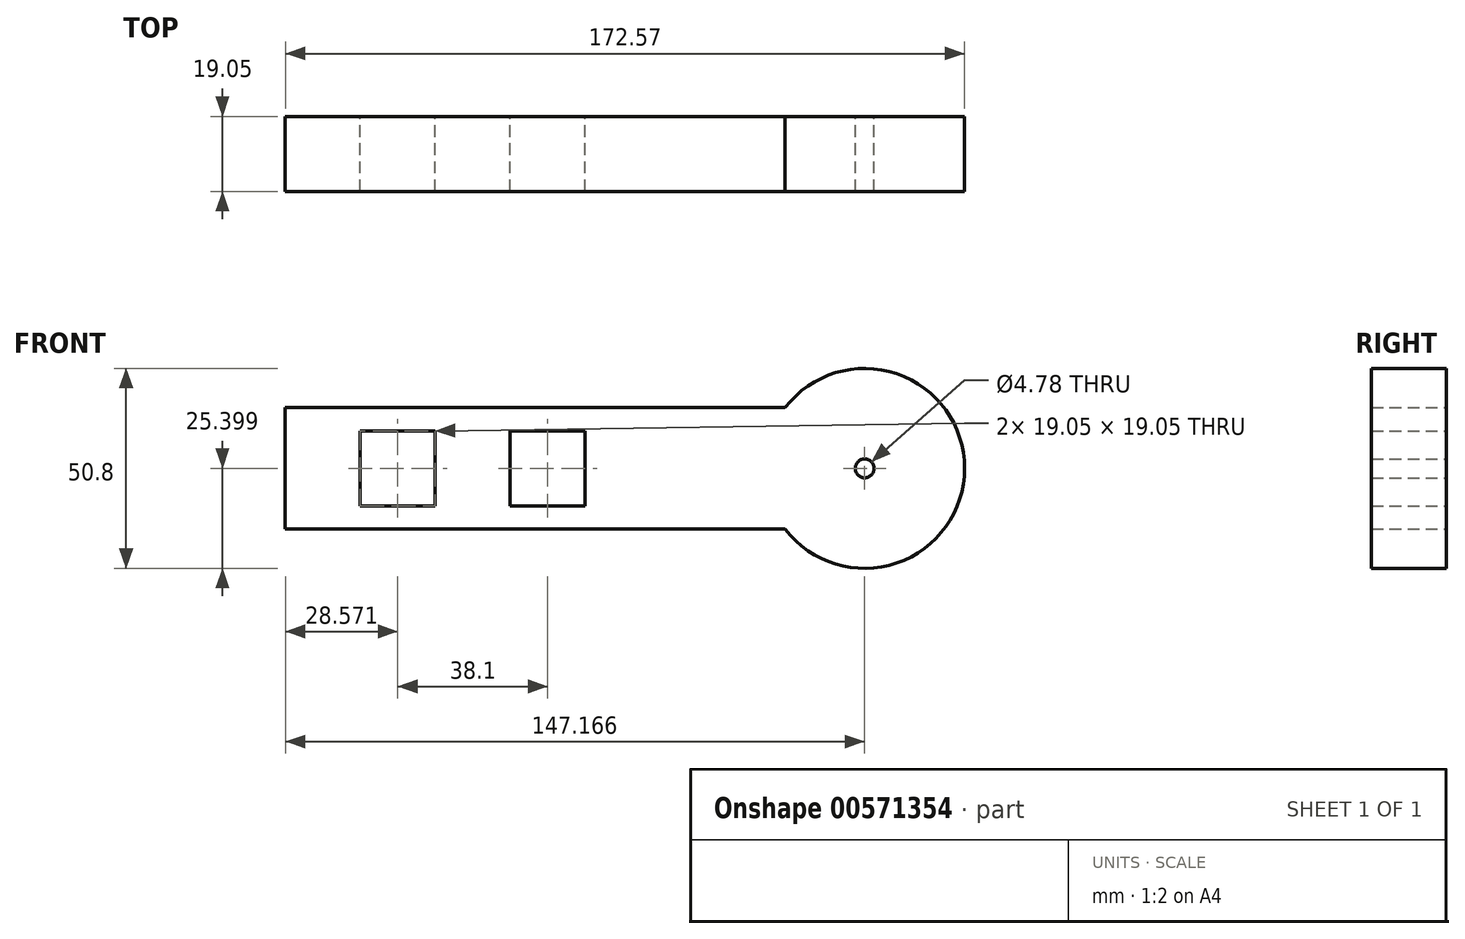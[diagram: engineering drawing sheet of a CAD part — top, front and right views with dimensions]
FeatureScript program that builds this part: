
annotation { "Feature Type Name" : "Feature", "Feature Type Description" : "" }
export const myFeature = defineFeature(function(context is Context, id is Id, definition is map)
    precondition{}
    {
        {
            var Q0;
            Q0=qCreatedBy(makeId("Front.planeOp"),FACE);
            var sketch = newSketch(context, id + "F0", { "sketchPlane" : qUnion([Q0])});
            skLineSegment(sketch, "E0", {"start": v(-146.45, -4.83) * mm, "end": v(-19.45, -4.83) * mm});
            skLineSegment(sketch, "E1", {"start": v(-19.45, -35.7) * mm, "end": v(-146.45, -35.7) * mm});
            skLineSegment(sketch, "E2", {"start": v(-146.45, -4.83) * mm, "end": v(-146.45, -35.7) * mm});
            skArc(sketch, "E3", {"start": v(-19.45, -35.7) * mm, "mid": v(26.12, -20.27) * mm, "end": v(-19.45, -4.83) * mm});
            skCircle(sketch, "E4", {"center": v(0.72, -20.27) * mm, "radius": 2.39 * mm});
            skLineSegment(sketch, "E5", {"start": v(-146.45, -20.27) * mm, "end": v(-63.2, -20.27) * mm});
            skLineSegment(sketch, "E6", {"start": v(-127.4, -20.27) * mm, "end": v(-127.4, -10.75) * mm});
            skLineSegment(sketch, "E7", {"start": v(-127.4, -10.75) * mm, "end": v(-108.35, -10.75) * mm});
            skLineSegment(sketch, "E8", {"start": v(-108.35, -10.75) * mm, "end": v(-108.35, -20.27) * mm});
            skLineSegment(sketch, "E9", {"start": v(-127.4, -20.27) * mm, "end": v(-127.4, -29.8) * mm});
            skLineSegment(sketch, "E10", {"start": v(-127.4, -29.8) * mm, "end": v(-108.35, -29.8) * mm});
            skLineSegment(sketch, "E11", {"start": v(-108.35, -29.8) * mm, "end": v(-108.35, -20.27) * mm});
            skLineSegment(sketch, "E12", {"start": v(-89.3, -20.27) * mm, "end": v(-89.3, -10.75) * mm});
            skLineSegment(sketch, "E13", {"start": v(-89.3, -10.75) * mm, "end": v(-70.25, -10.75) * mm});
            skLineSegment(sketch, "E14", {"start": v(-70.25, -10.75) * mm, "end": v(-70.25, -20.27) * mm});
            skLineSegment(sketch, "E15", {"start": v(-89.3, -20.27) * mm, "end": v(-89.3, -29.8) * mm});
            skLineSegment(sketch, "E16", {"start": v(-89.3, -29.8) * mm, "end": v(-70.25, -29.8) * mm});
            skLineSegment(sketch, "E17", {"start": v(-70.25, -29.8) * mm, "end": v(-70.25, -20.27) * mm});
            skLineSegment(sketch, "E18", {"start": v(-19.45, -4.83) * mm, "end": v(-19.45, -35.7) * mm});
            skSolve(sketch);
        }
        {
            var Q0;
            Q0=makeQuery(id+"F0.imprint","IMPRINT",FACE,{"disambiguationData":[TD([[makeQuery(id+"F0.imprint","IMPRINT",EDGE,{"derivedFrom":sQuery(id+"F0.wireOp",EDGE,"E0")}),-1.0]])]});
            var Q1;
            Q1=makeQuery(id+"F0.imprint","IMPRINT",FACE,{"disambiguationData":[TD([[makeQuery(id+"F0.imprint","IMPRINT",EDGE,{"derivedFrom":sQuery(id+"F0.wireOp",EDGE,"E3")}),1.0]])]});
            extrude(context, id + "F1", {"entities" : qUnion([Q0, Q1]), "depth" : 19.05 * mm, "offsetDistance" : 25.4 * mm});
        }
    });
